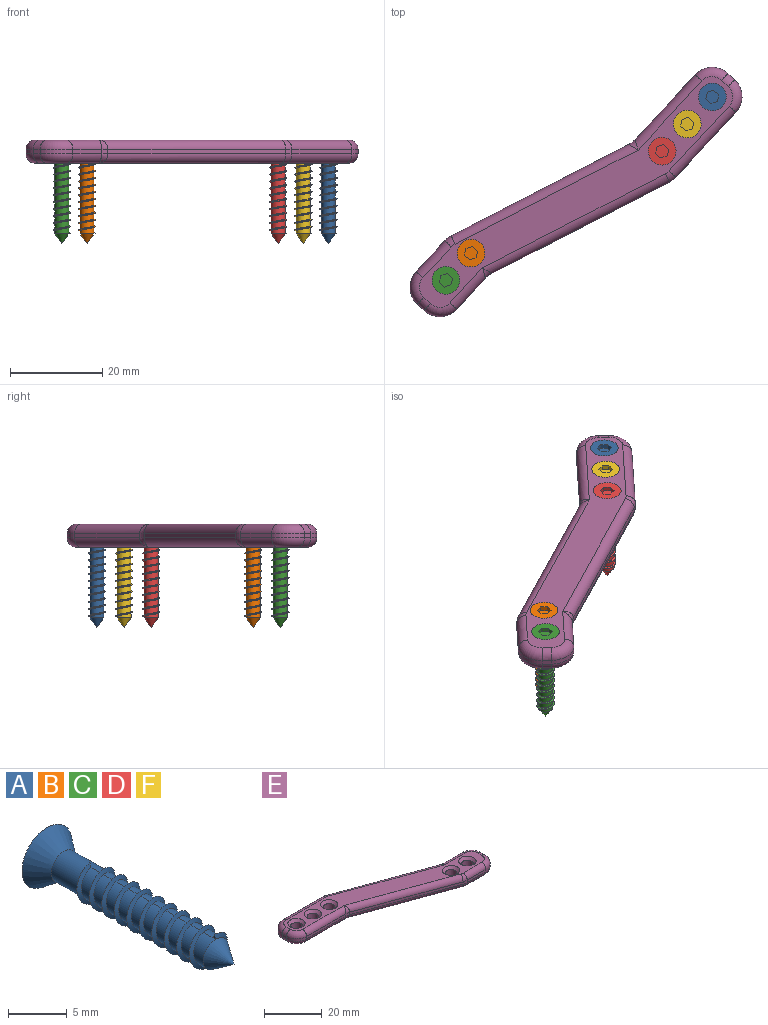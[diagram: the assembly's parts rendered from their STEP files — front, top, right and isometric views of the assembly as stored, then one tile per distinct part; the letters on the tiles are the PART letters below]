
ASSEMBLY  parts=6 mates=5
PART A: 25 faces, bbox 6x22.5x6 mm
  f0: plane 6x6mm, normal (0,1,0), area 22.4mm2, adj f1,f18,f19,f20,f21,f22,f23
  f1: cone r=3mm half-angle=36.9deg, axis (0,1,0), area 35.3mm2, adj f0,f2
  f2: cylinder r=1.5mm len=4.5mm, axis (0,1,0), area 35.3mm2, adj f1,f3,f13,f15
  f3: cylinder r=1.5mm len=3mm, axis (0,1,0), area 11.3mm2, adj f2,f4,f15,f16
  f4: cylinder r=1.5mm len=3mm, axis (0,1,0), area 11.3mm2, adj f3,f5,f15,f16
  f5: cylinder r=1.5mm len=3mm, axis (0,1,0), area 11.3mm2, adj f4,f6,f15,f16
  f6: cylinder r=1.5mm len=3mm, axis (0,1,0), area 11.3mm2, adj f5,f7,f15,f16
  f7: cylinder r=1.5mm len=3mm, axis (0,1,0), area 11.3mm2, adj f6,f8,f15,f16
  f8: cylinder r=1.5mm len=3mm, axis (0,1,0), area 11.3mm2, adj f7,f9,f15,f16
  f9: cylinder r=1.5mm len=3mm, axis (0,1,0), area 11.3mm2, adj f8,f10,f15,f16
  f10: cylinder r=1.5mm len=3mm, axis (0,1,0), area 11.3mm2, adj f9,f11,f15,f16
  f11: cylinder r=1.5mm len=3mm, axis (0,1,0), area 11.3mm2, adj f10,f12,f15,f16
  f12: cylinder r=1.5mm len=3mm, axis (0,1,0), area 7.1mm2, adj f11,f14,f16,f17
  f13: plane 0.4x0.3mm, normal (1,0,0), area 0.1mm2, adj f2,f15,f16
  f14: plane 0.4x0.3mm, normal (-1,0,0), area 0.1mm2, adj f12,f15,f16
  f15: bspline ~15.15x4.39mm, area 46mm2, adj f2,f3,f4,f5,f6,f7,f8,f9
  f16: bspline ~15.15x4.39mm, area 45.9mm2, adj f3,f4,f5,f6,f7,f8,f9,f10
  f17: cone r=1.5mm half-angle=34.3deg, axis (0,1,0), area 12.5mm2, adj f12
  f18: plane 1.5x1mm, normal (1,0,0), area 1.5mm2, adj f0,f19,f23,f24
  f19: plane 1.3x1mm, normal (0.5,0,-0.87), area 1.5mm2, adj f0,f18,f20,f24
  f20: plane 1.3x1mm, normal (-0.5,0,-0.87), area 1.5mm2, adj f0,f19,f21,f24
  f21: plane 1.5x1mm, normal (-1,0,0), area 1.5mm2, adj f0,f20,f22,f24
  f22: plane 1.3x1mm, normal (-0.5,0,0.87), area 1.5mm2, adj f0,f21,f23,f24
  f23: plane 1.3x1mm, normal (0.5,0,0.87), area 1.5mm2, adj f0,f18,f22,f24
  f24: plane 3x2.6mm, normal (0,1,0), area 5.8mm2, adj f18,f19,f20,f21,f22,f23
PART B: same geometry as A
PART C: same geometry as A
PART D: same geometry as A
PART E: 60 faces, bbox 83.1x28.2x5 mm
  f0: plane 78.29x23.39mm, normal (0,0,1), area 466.3mm2, adj f23,f24,f25,f26,f27,f28,f29,f30
  f1: plane 78.29x23.39mm, normal (0,0,-1), area 544.8mm2, adj f10,f11,f12,f13,f14,f15,f16,f17
  f2: plane 40.63x14.79mm, normal (0.34,0.94,0), area 43.2mm2, adj f19,f30,f47,f53
  f3: plane 19.12x1mm, normal (0,1,0), area 19.1mm2, adj f17,f28,f44,f47
  f4: plane 2x1mm, normal (-1,0,0), area 2mm2, adj f15,f26,f41,f44
  f5: plane 19.12x1mm, normal (0,-1,0), area 19.1mm2, adj f16,f24,f41,f50
  f6: plane 40.63x14.79mm, normal (-0.34,-0.94,0), area 43.2mm2, adj f18,f23,f38,f50
  f7: plane 9.12x1mm, normal (0,-1,0), area 9.1mm2, adj f20,f25,f35,f38
  f8: plane 2x1mm, normal (1,0,0), area 2mm2, adj f22,f27,f32,f35
  f9: plane 9.12x1mm, normal (0,1,0), area 9.1mm2, adj f21,f29,f32,f53
  f10: cylinder r=2mm len=4mm, axis (0,0,1), area 50.3mm2, adj f1,f58
  f11: cylinder r=2mm len=4mm, axis (0,0,1), area 50.3mm2, adj f1,f57
  f12: cylinder r=2mm len=4mm, axis (0,0,1), area 50.3mm2, adj f1,f59
  f13: cylinder r=2mm len=4mm, axis (0,0,1), area 50.3mm2, adj f1,f56
  f14: cylinder r=2mm len=4mm, axis (0,0,1), area 50.3mm2, adj f1,f55
  f15: cylinder r=2mm len=2mm, axis (0,-1,0), area 6.3mm2, adj f1,f4,f42,f45
  f16: cylinder r=2mm len=20.35mm, axis (1,0,0), area 61.5mm2, adj f1,f5,f42,f49
  f17: cylinder r=2mm len=19.12mm, axis (-1,0,0), area 60.1mm2, adj f1,f3,f45,f48
  f18: cylinder r=2mm len=42.47mm, axis (0.94,-0.34,0), area 137.2mm2, adj f1,f6,f39,f49
  f19: cylinder r=2mm len=42.47mm, axis (-0.94,0.34,0), area 137.2mm2, adj f1,f2,f48,f52
  f20: cylinder r=2mm len=9.12mm, axis (1,0,0), area 28.6mm2, adj f1,f7,f36,f39
  f21: cylinder r=2mm len=10.35mm, axis (-1,0,0), area 30.1mm2, adj f1,f9,f33,f52
  f22: cylinder r=2mm len=2mm, axis (0,1,0), area 6.3mm2, adj f1,f8,f33,f36
  f23: cylinder r=2mm len=42.47mm, axis (-0.94,0.34,0), area 137.2mm2, adj f0,f6,f37,f51
  f24: cylinder r=2mm len=20.35mm, axis (-1,0,0), area 61.5mm2, adj f0,f5,f40,f51
  f25: cylinder r=2mm len=9.12mm, axis (-1,0,0), area 28.6mm2, adj f0,f7,f34,f37
  f26: cylinder r=2mm len=2mm, axis (0,1,0), area 6.3mm2, adj f0,f4,f40,f43
  f27: cylinder r=2mm len=2mm, axis (0,-1,0), area 6.3mm2, adj f0,f8,f31,f34
  f28: cylinder r=2mm len=19.12mm, axis (1,0,0), area 60.1mm2, adj f0,f3,f43,f46
  f29: cylinder r=2mm len=10.35mm, axis (1,0,0), area 30.1mm2, adj f0,f9,f31,f54
  f30: cylinder r=2mm len=42.47mm, axis (0.94,-0.34,0), area 137.2mm2, adj f0,f2,f46,f54
  f31: torus R=3mm, axis (0,0,1), area 21.1mm2, adj f0,f27,f29,f32
  f32: cylinder r=5mm len=5mm, axis (0,0,1), area 7.9mm2, adj f8,f9,f31,f33
  f33: torus R=3mm, axis (0,0,1), area 21.1mm2, adj f1,f21,f22,f32
  f34: torus R=3mm, axis (0,0,1), area 21.1mm2, adj f0,f25,f27,f35
  f35: cylinder r=5mm len=5mm, axis (0,0,-1), area 7.9mm2, adj f7,f8,f34,f36
  f36: torus R=3mm, axis (0,0,1), area 21.1mm2, adj f1,f20,f22,f35
  f37: torus R=3mm, axis (0,0,1), area 4.7mm2, adj f0,f23,f25,f38
  f38: cylinder r=5mm len=1.71mm, axis (0,0,-1), area 1.7mm2, adj f6,f7,f37,f39
  f39: torus R=3mm, axis (0,0,1), area 4.7mm2, adj f1,f18,f20,f38
  f40: torus R=3mm, axis (0,0,1), area 21.1mm2, adj f0,f24,f26,f41
  f41: cylinder r=5mm len=5mm, axis (0,0,1), area 7.9mm2, adj f4,f5,f40,f42
  f42: torus R=3mm, axis (0,0,1), area 21.1mm2, adj f1,f15,f16,f41
  f43: torus R=3mm, axis (0,0,1), area 21.1mm2, adj f0,f26,f28,f44
  f44: cylinder r=5mm len=5mm, axis (0,0,-1), area 7.9mm2, adj f3,f4,f43,f45
  f45: torus R=3mm, axis (0,0,1), area 21.1mm2, adj f1,f15,f17,f44
  f46: torus R=3mm, axis (0,0,1), area 4.7mm2, adj f0,f28,f30,f47
  f47: cylinder r=5mm len=1.71mm, axis (0,0,-1), area 1.7mm2, adj f2,f3,f46,f48
  f48: torus R=3mm, axis (0,0,1), area 4.7mm2, adj f1,f17,f19,f47
  f49: bspline ~2.3x2.26mm, area 3.5mm2, adj f16,f18,f50
  f50: cylinder r=5mm len=1.71mm, axis (0,0,1), area 1.7mm2, adj f5,f6,f49,f51
  f51: bspline ~2.3x2.26mm, area 3.5mm2, adj f23,f24,f50
  f52: bspline ~2.3x2.26mm, area 3.5mm2, adj f19,f21,f53
  f53: cylinder r=5mm len=1.71mm, axis (0,0,1), area 1.7mm2, adj f2,f9,f52,f54
  f54: bspline ~2.3x2.26mm, area 3.5mm2, adj f29,f30,f53
  f55: cone r=2mm half-angle=45deg, axis (0,0,1), area 22.2mm2, adj f0,f14
  f56: cone r=2mm half-angle=45deg, axis (0,0,1), area 22.2mm2, adj f0,f13
  f57: cone r=2mm half-angle=45deg, axis (0,0,1), area 22.2mm2, adj f0,f11
  f58: cone r=2mm half-angle=45deg, axis (0,0,1), area 22.2mm2, adj f0,f10
  f59: cone r=2mm half-angle=45deg, axis (0,0,1), area 22.2mm2, adj f0,f12
PART F: same geometry as A
PLACE A rot(axis=(0.46,0.63,0.63),130.4deg) t=(58.67,63.93,112.77)mm
PLACE B rot(axis=(0.46,0.63,0.63),130.4deg) t=(6.44,30.13,112.77)mm
PLACE C rot(axis=(0.46,0.63,0.63),130.4deg) t=(1,24.25,112.77)mm
PLACE D rot(axis=(0.46,0.63,0.63),130.4deg) t=(47.81,52.19,112.77)mm
PLACE E rot(axis=(0,0,-1),132.8deg) t=(58.34,72.41,107.77)mm
PLACE F rot(axis=(0.46,0.63,0.63),130.4deg) t=(53.24,58.06,112.77)mm
MATE cylindrical A.f1 <-> E.f11  axis (0,0,1) through (58.67,63.93,110.77)mm
MATE cylindrical F.f1 <-> E.f10  axis (0,0,1) through (53.24,58.06,110.77)mm
MATE cylindrical B.f1 <-> E.f13  axis (0,0,1) through (6.44,30.13,110.77)mm
MATE cylindrical C.f1 <-> E.f14  axis (0,0,1) through (1,24.25,110.77)mm
MATE cylindrical D.f1 <-> E.f12  axis (0,0,1) through (47.81,52.19,110.77)mm
